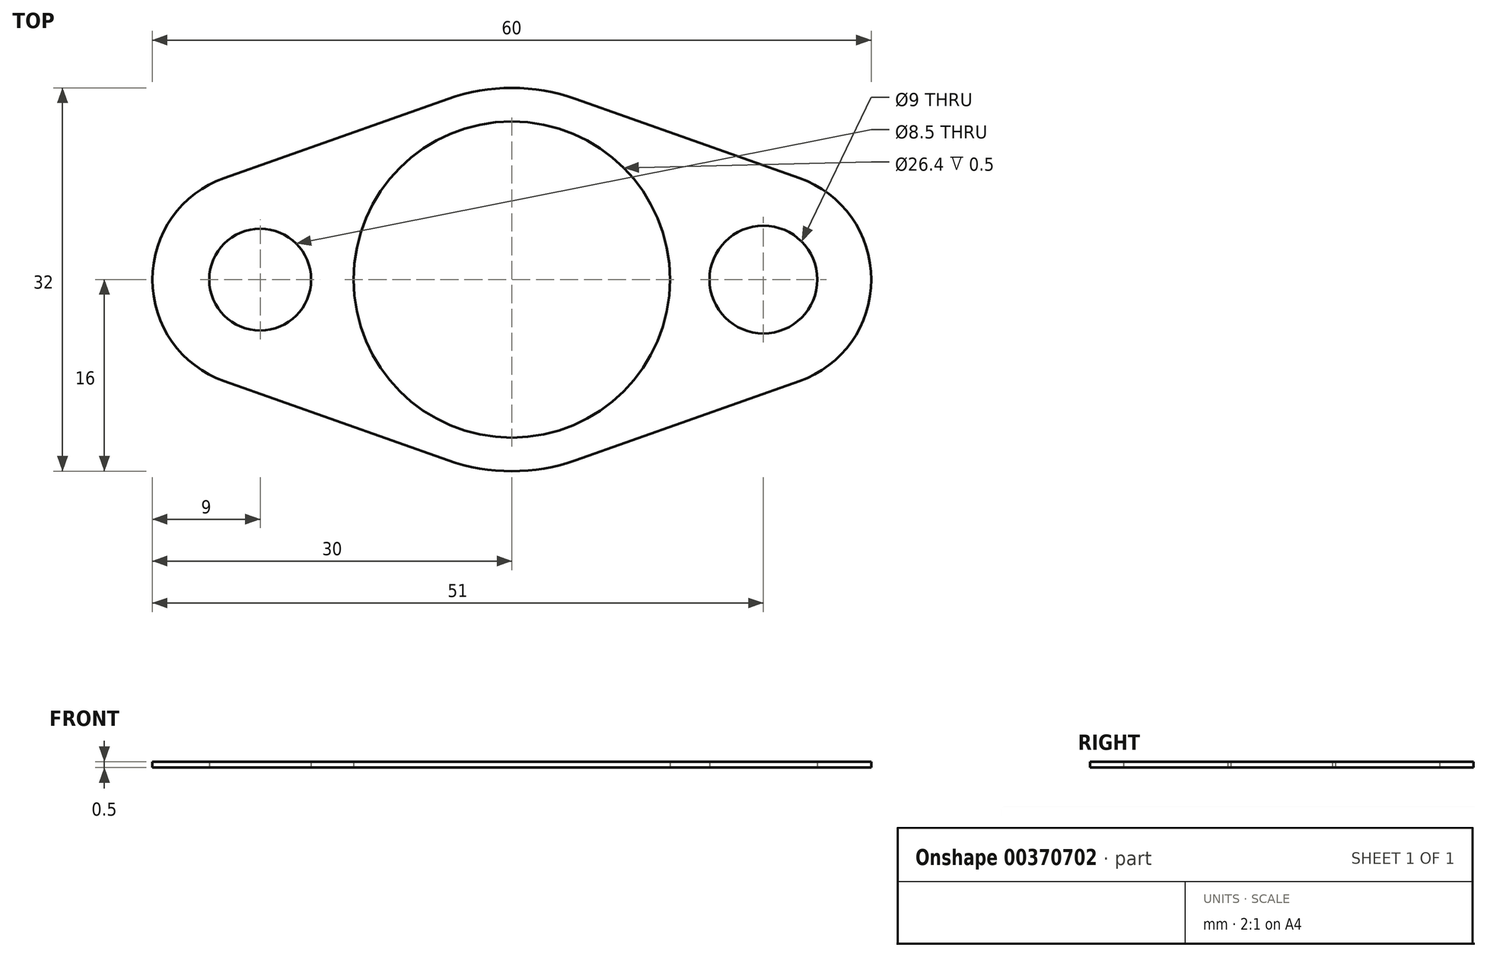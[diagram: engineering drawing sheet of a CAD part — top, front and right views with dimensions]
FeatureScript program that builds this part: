
annotation { "Feature Type Name" : "Feature", "Feature Type Description" : "" }
export const myFeature = defineFeature(function(context is Context, id is Id, definition is map)
    precondition{}
    {
        {
            var Q0;
            Q0=qCreatedBy(makeId("Top.planeOp"),FACE);
            var sketch = newSketch(context, id + "F0", { "sketchPlane" : qUnion([Q0])});
            skCircle(sketch, "E0", {"center": v(0, 0) * mm, "radius": 13.2 * mm});
            skSolve(sketch);
        }
        {
            var Q0;
            Q0=makeQuery(id+"F0.imprint","IMPRINT",FACE,{"disambiguationData":[TD([[makeQuery(id+"F0.imprint","IMPRINT",EDGE,{"derivedFrom":sQuery(id+"F0.wireOp",EDGE,"E0")}),1.0]])]});
            var sketch = newSketch(context, id + "F1", { "sketchPlane" : qUnion([Q0])});
            skArc(sketch, "E1", {"start": v(-5.33, -15.08) * mm, "mid": v(0, -16) * mm, "end": v(5.33, -15.08) * mm});
            skCircle(sketch, "E2", {"center": v(-21, 0) * mm, "radius": 4.25 * mm});
            skCircle(sketch, "E3", {"center": v(21, 0) * mm, "radius": 4.5 * mm});
            skArc(sketch, "E4.trimOffspring", {"start": v(5.33, 15.08) * mm, "mid": v(0, 16) * mm, "end": v(-5.33, 15.08) * mm});
            skArc(sketch, "E5", {"start": v(-24, 8.49) * mm, "mid": v(-30, 0) * mm, "end": v(-24, -8.49) * mm});
            skLineSegment(sketch, "E6", {"start": v(-24, -8.49) * mm, "end": v(-5.33, -15.08) * mm});
            skLineSegment(sketch, "E7", {"start": v(-24, 8.49) * mm, "end": v(-5.33, 15.08) * mm});
            skPoint(sketch, "E8.orphan", {"position": v(-7.24, 14.27) * mm});
            skPoint(sketch, "E9.orphan", {"position": v(-7.24, -14.27) * mm});
            skArc(sketch, "E10", {"start": v(24, -8.49) * mm, "mid": v(30, 0) * mm, "end": v(24, 8.49) * mm});
            skLineSegment(sketch, "E11", {"start": v(24, 8.49) * mm, "end": v(5.33, 15.08) * mm});
            skLineSegment(sketch, "E12", {"start": v(24, -8.49) * mm, "end": v(5.33, -15.08) * mm});
            skPoint(sketch, "E13.orphan", {"position": v(7.24, 14.27) * mm});
            skPoint(sketch, "E14.orphan", {"position": v(7.24, -14.27) * mm});
            skSolve(sketch);
        }
        {
            var Q0;
            Q0=makeQuery(id+"F1.imprint","IMPRINT",FACE,{"disambiguationData":[TD([[makeQuery(id+"F1.imprint","IMPRINT",EDGE,{"derivedFrom":sQuery(id+"F1.wireOp",EDGE,"E1")}),1.0]])]});
            extrude(context, id + "F2", {"entities" : qUnion([Q0]), "depth" : 0.5 * mm, "offsetDistance" : 25 * mm});
        }
    });
